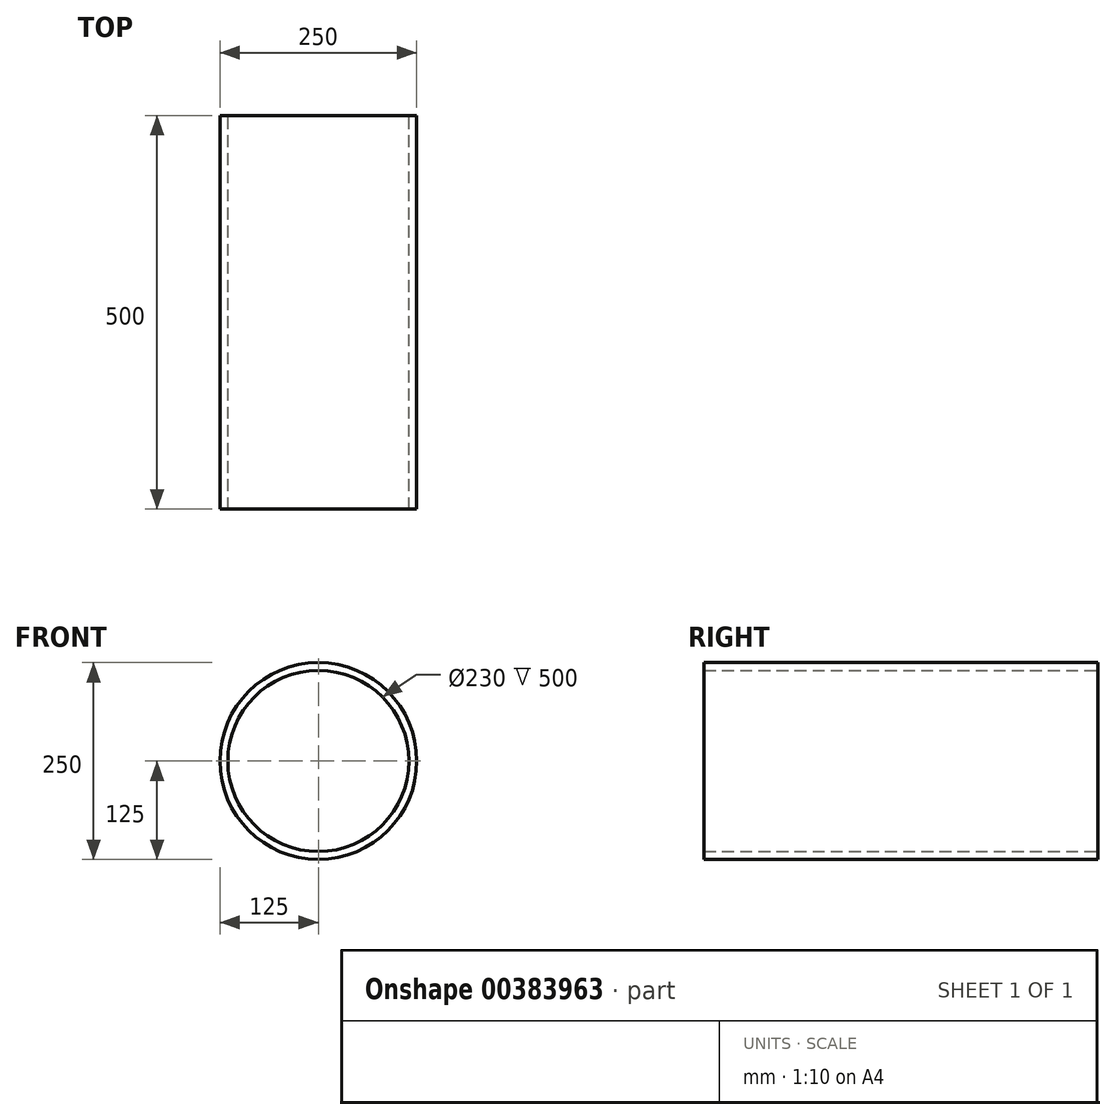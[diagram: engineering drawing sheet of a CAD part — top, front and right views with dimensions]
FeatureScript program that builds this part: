
annotation { "Feature Type Name" : "Feature", "Feature Type Description" : "" }
export const myFeature = defineFeature(function(context is Context, id is Id, definition is map)
    precondition{}
    {
        {
            var Q0;
            Q0=qCreatedBy(makeId("Front.planeOp"),FACE);
            var sketch = newSketch(context, id + "F0", { "sketchPlane" : qUnion([Q0])});
            skCircle(sketch, "E0", {"center": v(0, 0) * mm, "radius": 125 * mm});
            skSolve(sketch);
        }
        {
            var Q0;
            Q0=qSketchRegion(id+"F0",true);
            extrude(context, id + "F1", {"entities" : qUnion([Q0]), "depth" : 500 * mm});
        }
        {
            var Q0;
            Q0=makeQuery(id+"F1.opExtrude","CAP_FACE",FACE,{"disambiguationData":[OSD([sQuery(id+"F0.wireOp",EDGE,"E0")])],"isStart":false});
            var Q1;
            Q1=makeQuery(id+"F1.opExtrude","CAP_FACE",FACE,{"disambiguationData":[OSD([sQuery(id+"F0.wireOp",EDGE,"E0")])],"isStart":true});
            var Q2;
            Q2=makeQuery(id+"F1.opExtrude","SWEPT_BODY",BODY,{"disambiguationData":[OSD([sQuery(id+"FF9Xk7hbtk2z74Y_0.wireOp",EDGE,"4NDKS2yC-K3nY-Xg0L-782P-uufcIwUOuggp")])]});
            shell(context, id + "F2", {"entities" : qUnion([Q0, Q1]), "parts" : qUnion([Q2]), "thickness" : 10 * mm});
        }
    });
